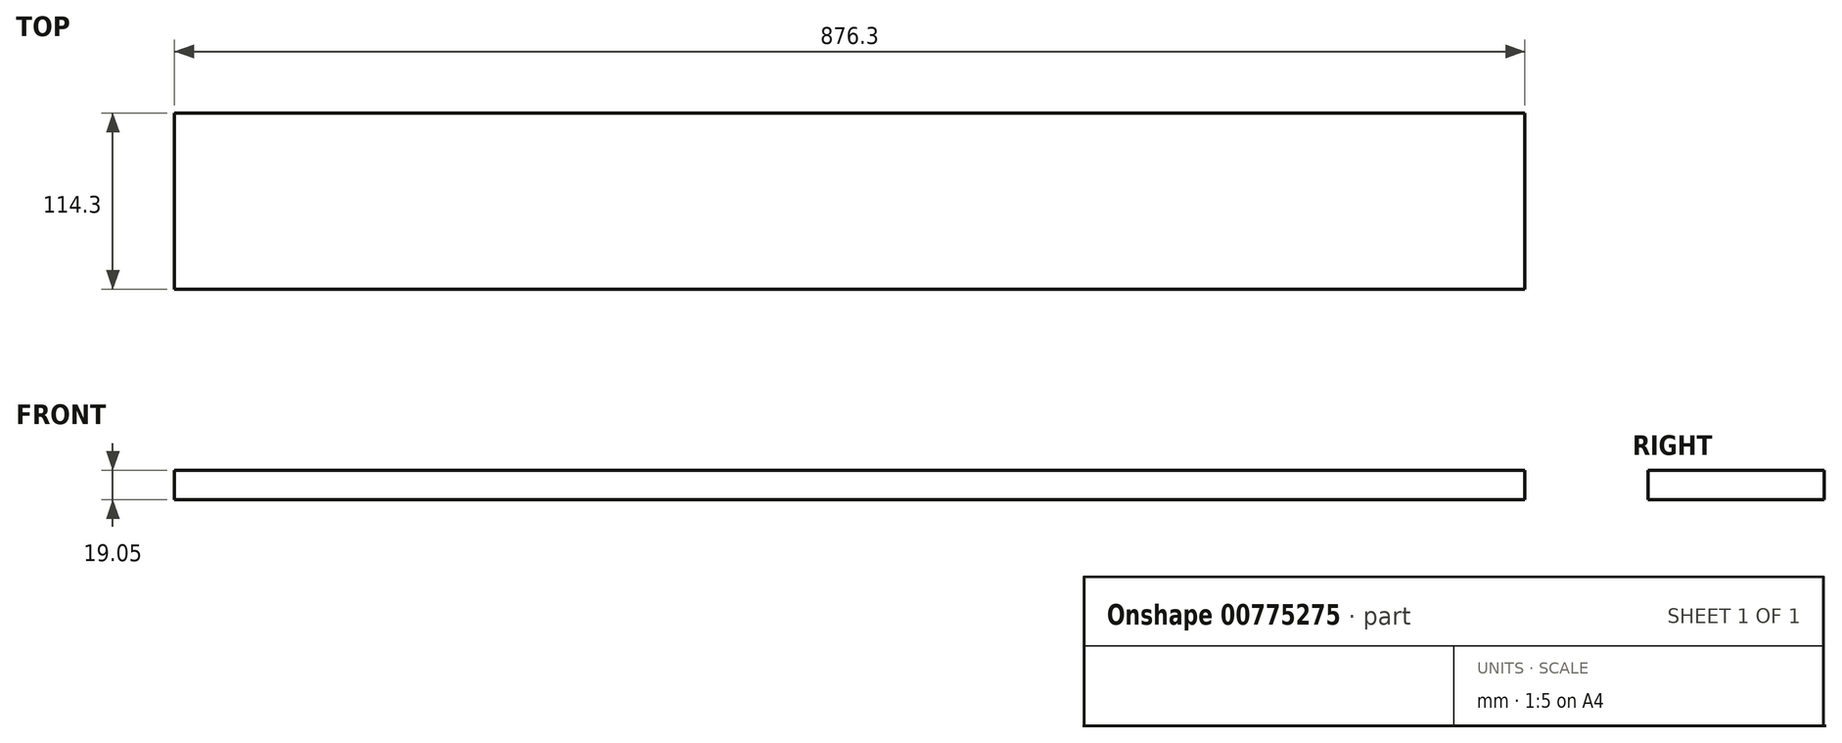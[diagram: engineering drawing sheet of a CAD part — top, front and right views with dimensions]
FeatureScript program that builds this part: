
annotation { "Feature Type Name" : "Feature", "Feature Type Description" : "" }
export const myFeature = defineFeature(function(context is Context, id is Id, definition is map)
    precondition{}
    {
        {
            var Q0;
            Q0=qCreatedBy(makeId("Top.planeOp"),FACE);
            var sketch = newSketch(context, id + "F0", { "sketchPlane" : qUnion([Q0])});
            skLineSegment(sketch, "E0.bottom", {"start": v(0, 0) * mm, "end": v(-876.3, 0) * mm});
            skLineSegment(sketch, "E0.top", {"start": v(0, 114.3) * mm, "end": v(-876.3, 114.3) * mm});
            skLineSegment(sketch, "E0.left", {"start": v(0, 0) * mm, "end": v(0, 114.3) * mm});
            skLineSegment(sketch, "E0.right", {"start": v(-876.3, 0) * mm, "end": v(-876.3, 114.3) * mm});
            skSolve(sketch);
        }
        {
            var Q0;
            Q0 = qSketchRegion(id + "F0", true);
            extrude(context, id + "F1", {"entities" : qUnion([Q0]), "depth" : 19.05 * mm, "offsetDistance" : 25.4 * mm});
        }
    });
